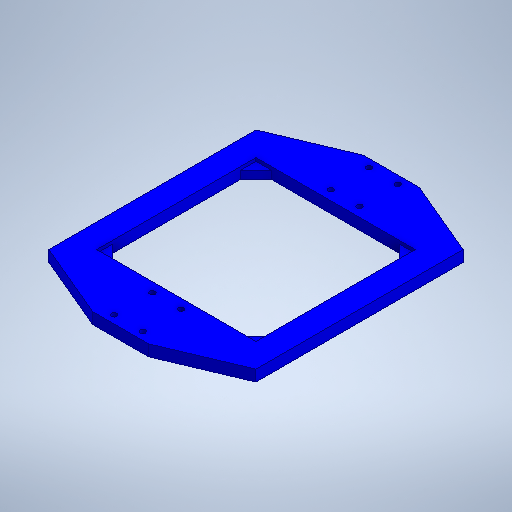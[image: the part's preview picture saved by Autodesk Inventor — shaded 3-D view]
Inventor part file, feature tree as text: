
AUTODESK INVENTOR PART (.ipt)
format: ipt  version: 2025.2 (Build 292293000, 293)  size: 294,912 bytes
history: native  units: mm
features: extrude x2, sketch x1, hole x1
ambient origin geometry x8: Origin, YZ Plane, XZ Plane, XY Plane, X Axis, Y Axis, Z Axis, Center Point
bodies: Solid1 (feature_tree)
feature tree (4):
  sketch  "Sketch1"  dims[d0=100.0mm d1=100.0mm d4=130.0mm d5=170.0mm d6=20.0mm d7=40.0mm d8=40.0mm d10=7.5mm d11=7.5mm d12=20.0mm d13=47.5mm d14=10.0mm d15=10.0mm d16=10.0mm d17=10.0mm d18=5.0mm d19=0.0mm d20=2.0mm d21=0.0mm d22=5.0mm d23=18.0mm d24=24.0mm d25=5.0mm d26=18.0mm d27=24.0mm d28=3.4mm d29=6.0mm d30=4.0mm d31=2.0mm d32=90.0deg d33=8.0mm d34=20.594885mm]
  extrude  "Extrusion1"  Depth=100.0mm
  extrude  "Extrusion2"  Depth=130.0mm
  hole  "Hole1"  [1 undecoded]
note: 1 required parameter value undecoded (feature->parameter linkage not recoverable at this tier; creation-order binding heuristic only, values carry confidence <= 0.55)
